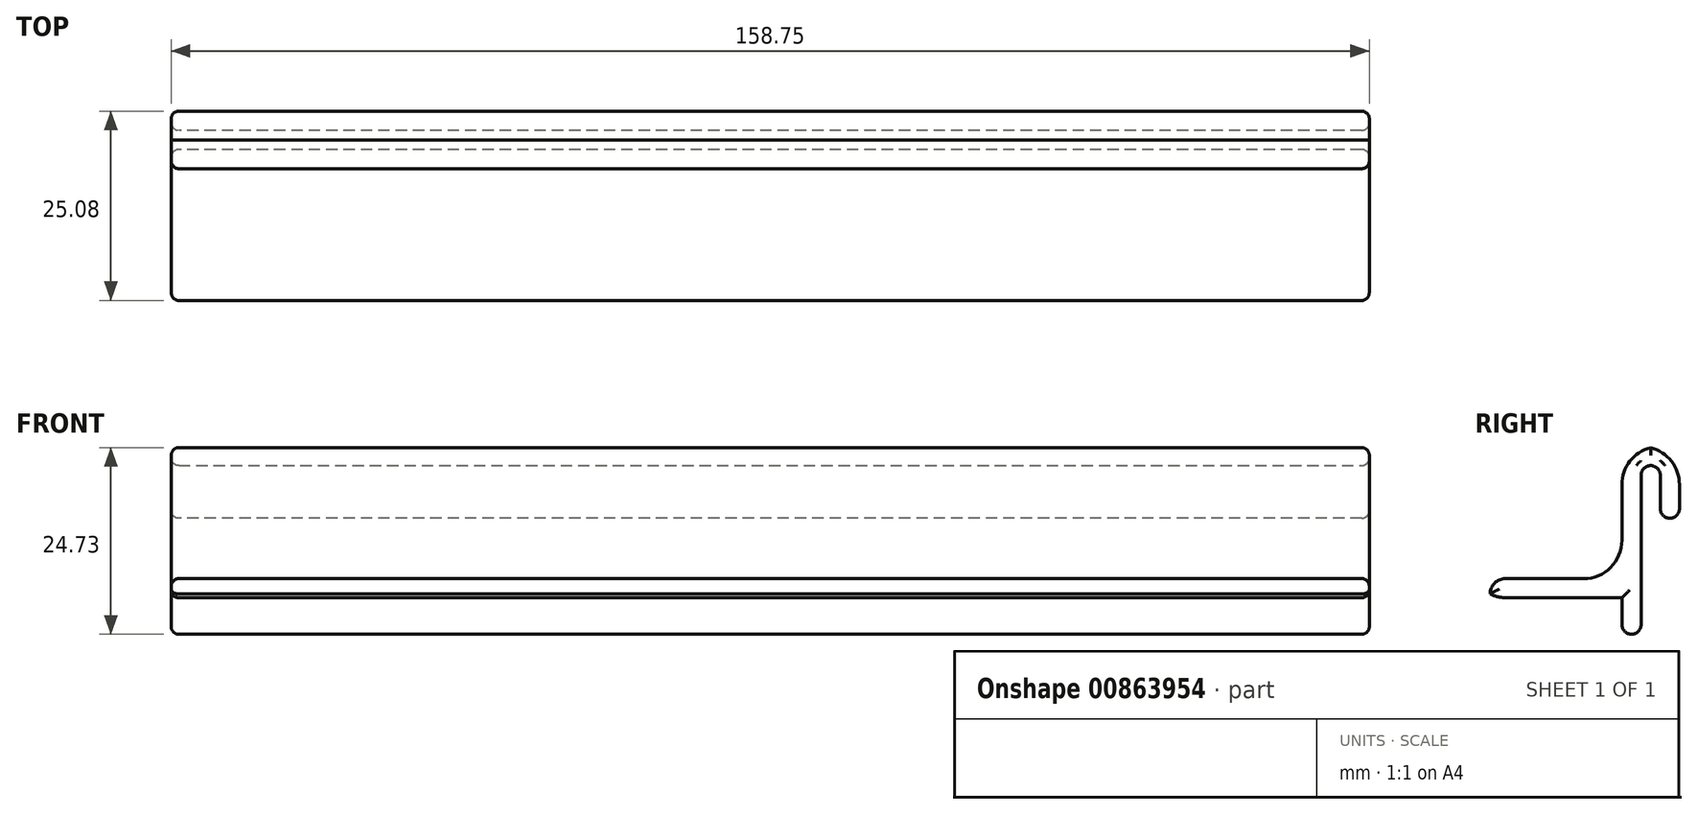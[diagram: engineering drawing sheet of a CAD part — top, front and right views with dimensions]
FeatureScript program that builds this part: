
annotation { "Feature Type Name" : "Feature", "Feature Type Description" : "" }
export const myFeature = defineFeature(function(context is Context, id is Id, definition is map)
    precondition{}
    {
        {
            var Q0;
            Q0=qCreatedBy(makeId("Right.planeOp"),FACE);
            var sketch = newSketch(context, id + "F0", { "sketchPlane" : qUnion([Q0])});
            skLineSegment(sketch, "E0", {"start": v(0, 0) * mm, "end": v(-17.46, 0) * mm});
            skLineSegment(sketch, "E1", {"start": v(-17.46, 0) * mm, "end": v(-17.46, -2.54) * mm});
            skLineSegment(sketch, "E2", {"start": v(-17.46, -2.54) * mm, "end": v(0, -2.54) * mm});
            skLineSegment(sketch, "E3", {"start": v(0, -2.54) * mm, "end": v(0, -7.37) * mm});
            skLineSegment(sketch, "E4", {"start": v(0, -7.37) * mm, "end": v(2.54, -7.37) * mm});
            skLineSegment(sketch, "E5", {"start": v(2.54, -7.37) * mm, "end": v(2.54, 14.99) * mm});
            skLineSegment(sketch, "E6", {"start": v(2.54, 14.99) * mm, "end": v(5.08, 14.99) * mm});
            skLineSegment(sketch, "E7", {"start": v(5.08, 14.99) * mm, "end": v(5.08, 8) * mm});
            skLineSegment(sketch, "E8", {"start": v(5.08, 8) * mm, "end": v(7.62, 8) * mm});
            skLineSegment(sketch, "E9", {"start": v(7.62, 8) * mm, "end": v(7.62, 17.53) * mm});
            skLineSegment(sketch, "E10", {"start": v(7.62, 17.53) * mm, "end": v(0, 17.53) * mm});
            skLineSegment(sketch, "E11", {"start": v(0, 17.53) * mm, "end": v(0, 0) * mm});
            skSolve(sketch);
        }
        {
            var Q0;
            Q0 = qSketchRegion(id + "F0", true);
            extrude(context, id + "F1", {"entities" : qUnion([Q0]), "depth" : 158.75 * mm, "offsetDistance" : 25.4 * mm});
        }
        {
            var Q0;
            Q0=makeQuery(id+"F1.opExtrude","SWEPT_EDGE",EDGE,{"disambiguationData":[OSD([sQuery(id+"F0.wireOp",EDGE,"E0"),sQuery(id+"F0.wireOp",EDGE,"E1")])]});
            fillet(context, id + "F2", {"entities" : qUnion([Q0]), "radius" : 2.03 * mm, "tangentPropagation" : true, "allowEdgeOverflow" : false});
        }
        {
            var Q0;
            Q0=makeQuery(id+"F1.opExtrude","SWEPT_EDGE",EDGE,{"disambiguationData":[OSD([sQuery(id+"F0.wireOp",EDGE,"E5"),sQuery(id+"F0.wireOp",EDGE,"E6")])]});
            var Q1;
            Q1=makeQuery(id+"F1.opExtrude","SWEPT_EDGE",EDGE,{"disambiguationData":[OSD([sQuery(id+"F0.wireOp",EDGE,"E6"),sQuery(id+"F0.wireOp",EDGE,"E7")])]});
            var Q2;
            Q2=makeQuery(id+"F1.opExtrude","SWEPT_EDGE",EDGE,{"disambiguationData":[OSD([sQuery(id+"F0.wireOp",EDGE,"E7"),sQuery(id+"F0.wireOp",EDGE,"E8")])]});
            var Q3;
            Q3=makeQuery(id+"F1.opExtrude","SWEPT_EDGE",EDGE,{"disambiguationData":[OSD([sQuery(id+"F0.wireOp",EDGE,"E8"),sQuery(id+"F0.wireOp",EDGE,"E9")])]});
            var Q4;
            Q4=makeQuery(id+"F1.opExtrude","SWEPT_EDGE",EDGE,{"disambiguationData":[OSD([sQuery(id+"F0.wireOp",EDGE,"E4"),sQuery(id+"F0.wireOp",EDGE,"E5")])]});
            var Q5;
            Q5=makeQuery(id+"F1.opExtrude","SWEPT_EDGE",EDGE,{"disambiguationData":[OSD([sQuery(id+"F0.wireOp",EDGE,"E3"),sQuery(id+"F0.wireOp",EDGE,"E4")])]});
            fillet(context, id + "F3", {"entities" : qUnion([Q0, Q1, Q2, Q3, Q4, Q5]), "radius" : 1.27 * mm, "tangentPropagation" : true, "allowEdgeOverflow" : false});
        }
        {
            var Q0;
            Q0=makeQuery(id+"F1.opExtrude","SWEPT_EDGE",EDGE,{"disambiguationData":[OSD([sQuery(id+"F0.wireOp",EDGE,"E1"),sQuery(id+"F0.wireOp",EDGE,"E2")])]});
            fillet(context, id + "F4", {"entities" : qUnion([Q0]), "radius" : 5.08 * mm, "tangentPropagation" : true, "allowEdgeOverflow" : false});
        }
        {
            var Q0;
            Q0=makeQuery(id+"F1.opExtrude","SWEPT_EDGE",EDGE,{"disambiguationData":[OSD([sQuery(id+"F0.wireOp",EDGE,"E10"),sQuery(id+"F0.wireOp",EDGE,"E11")])]});
            var Q1;
            Q1=makeQuery(id+"F1.opExtrude","SWEPT_EDGE",EDGE,{"disambiguationData":[OSD([sQuery(id+"F0.wireOp",EDGE,"E9"),sQuery(id+"F0.wireOp",EDGE,"E10")])]});
            var Q2;
            Q2=makeQuery(id+"F1.opExtrude","SWEPT_EDGE",EDGE,{"disambiguationData":[OSD([sQuery(id+"F0.wireOp",EDGE,"E0"),sQuery(id+"F0.wireOp",EDGE,"E11")])]});
            fillet(context, id + "F5", {"entities" : qUnion([Q0, Q1, Q2]), "radius" : 5.08 * mm, "tangentPropagation" : true, "allowEdgeOverflow" : false});
        }
        {
            var Q0;
            Q0=makeQuery(id+"F1.opExtrude","CAP_FACE",FACE,{"disambiguationData":[OSD([sQuery(id+"F0.wireOp",EDGE,"E0"),sQuery(id+"F0.wireOp",EDGE,"E1"),sQuery(id+"F0.wireOp",EDGE,"E2"),sQuery(id+"F0.wireOp",EDGE,"E3"),sQuery(id+"F0.wireOp",EDGE,"E4"),sQuery(id+"F0.wireOp",EDGE,"E5"),sQuery(id+"F0.wireOp",EDGE,"E6"),sQuery(id+"F0.wireOp",EDGE,"E7"),sQuery(id+"F0.wireOp",EDGE,"E8"),sQuery(id+"F0.wireOp",EDGE,"E9"),sQuery(id+"F0.wireOp",EDGE,"E10"),sQuery(id+"F0.wireOp",EDGE,"E11")])],"isStart":false});
            var Q1;
            Q1=makeQuery(id+"F1.opExtrude","CAP_FACE",FACE,{"disambiguationData":[OSD([sQuery(id+"F0.wireOp",EDGE,"E0"),sQuery(id+"F0.wireOp",EDGE,"E1"),sQuery(id+"F0.wireOp",EDGE,"E2"),sQuery(id+"F0.wireOp",EDGE,"E3"),sQuery(id+"F0.wireOp",EDGE,"E4"),sQuery(id+"F0.wireOp",EDGE,"E5"),sQuery(id+"F0.wireOp",EDGE,"E6"),sQuery(id+"F0.wireOp",EDGE,"E7"),sQuery(id+"F0.wireOp",EDGE,"E8"),sQuery(id+"F0.wireOp",EDGE,"E9"),sQuery(id+"F0.wireOp",EDGE,"E10"),sQuery(id+"F0.wireOp",EDGE,"E11")])],"isStart":true});
            fillet(context, id + "F6", {"entities" : qUnion([Q0, Q1]), "radius" : 1.02 * mm, "tangentPropagation" : true, "allowEdgeOverflow" : false});
        }
    });
